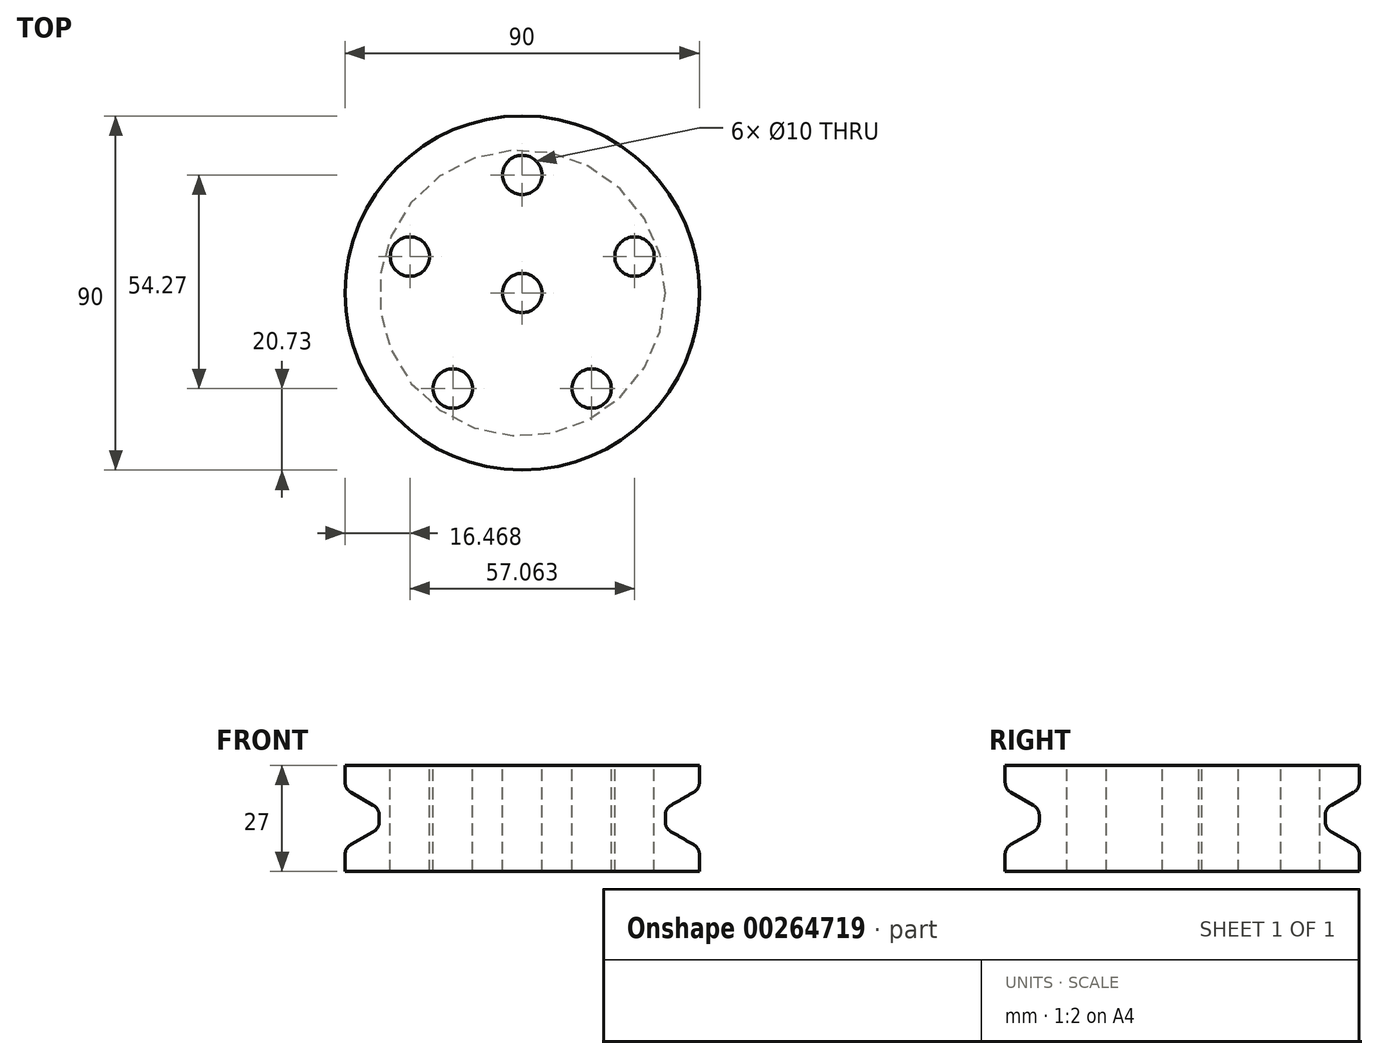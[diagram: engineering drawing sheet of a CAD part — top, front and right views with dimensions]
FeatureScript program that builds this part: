
annotation { "Feature Type Name" : "Feature", "Feature Type Description" : "" }
export const myFeature = defineFeature(function(context is Context, id is Id, definition is map)
    precondition{}
    {
        {
            var Q0;
            Q0=qCreatedBy(makeId("Front.planeOp"),FACE);
            var sketch = newSketch(context, id + "F0", { "sketchPlane" : qUnion([Q0])});
            skLineSegment(sketch, "E0", {"start": v(0, 18.67) * mm, "end": v(0, -19.25) * mm, "construction": true});
            skLineSegment(sketch, "E1", {"start": v(-5, 11.04) * mm, "end": v(-45, 11.04) * mm});
            skLineSegment(sketch, "E2", {"start": v(-45, 11.04) * mm, "end": v(-45, 5.04) * mm});
            skLineSegment(sketch, "E3", {"start": v(-45, 5.04) * mm, "end": v(-36.34, 0.04) * mm});
            skLineSegment(sketch, "E4", {"start": v(-36.34, 0.04) * mm, "end": v(-36.34, -4.96) * mm});
            skLineSegment(sketch, "E5", {"start": v(-36.34, -4.96) * mm, "end": v(-45, -9.96) * mm});
            skLineSegment(sketch, "E6", {"start": v(-45, -9.96) * mm, "end": v(-45, -15.96) * mm});
            skLineSegment(sketch, "E7", {"start": v(-45, -15.96) * mm, "end": v(-5, -15.96) * mm});
            skLineSegment(sketch, "E8", {"start": v(-5, -15.96) * mm, "end": v(-5, 11.04) * mm});
            skSolve(sketch);
        }
        {
            var Q0;
            Q0=makeQuery(id+"F0.imprint","IMPRINT",FACE,{"disambiguationData":[TD([[makeQuery(id+"F0.imprint","IMPRINT",EDGE,{"derivedFrom":sQuery(id+"F0.wireOp",EDGE,"E1")}),1.0]])]});
            var Q1;
            Q1=sQuery(id+"F0.wireOp",EDGE,"E0");
            revolve(context, id + "F1", {"entities" : qUnion([Q0]), "axis" : qUnion([Q1]), "revolveType" : RevolveType.FULL});
        }
        {
            var Q0;
            Q0=makeQuery(id+"F1.opRevolve","SWEPT_FACE",FACE,{"disambiguationData":[OSD([sQuery(id+"F0.wireOp",EDGE,"E1")])]});
            var sketch = newSketch(context, id + "F2", { "sketchPlane" : qUnion([Q0])});
            skCircle(sketch, "E9", {"center": v(0, 30) * mm, "radius": 5 * mm});
            skCircle(sketch, "E10.1.0", {"center": v(-28.53, 9.27) * mm, "radius": 5 * mm});
            skCircle(sketch, "E10.2.0", {"center": v(-17.63, -24.27) * mm, "radius": 5 * mm});
            skCircle(sketch, "E10.3.0", {"center": v(17.63, -24.27) * mm, "radius": 5 * mm});
            skCircle(sketch, "E10.4.0", {"center": v(28.53, 9.27) * mm, "radius": 5 * mm});
            skPoint(sketch, "E10.center", {"position": v(0, 0) * mm});
            skSolve(sketch);
        }
        {
            var Q0;
            Q0=makeQuery(id+"F2.imprint","IMPRINT",FACE,{"disambiguationData":[TD([[makeQuery(id+"F2.imprint","IMPRINT",EDGE,{"derivedFrom":sQuery(id+"F2.wireOp",EDGE,"E10.2.0")}),1.0]])]});
            var Q1;
            Q1=makeQuery(id+"F2.imprint","IMPRINT",FACE,{"disambiguationData":[TD([[makeQuery(id+"F2.imprint","IMPRINT",EDGE,{"derivedFrom":sQuery(id+"F2.wireOp",EDGE,"E10.1.0")}),1.0]])]});
            var Q2;
            Q2=makeQuery(id+"F2.imprint","IMPRINT",FACE,{"disambiguationData":[TD([[makeQuery(id+"F2.imprint","IMPRINT",EDGE,{"derivedFrom":sQuery(id+"F2.wireOp",EDGE,"E9")}),1.0]])]});
            var Q3;
            Q3=makeQuery(id+"F2.imprint","IMPRINT",FACE,{"disambiguationData":[TD([[makeQuery(id+"F2.imprint","IMPRINT",EDGE,{"derivedFrom":sQuery(id+"F2.wireOp",EDGE,"E10.4.0")}),1.0]])]});
            var Q4;
            Q4=makeQuery(id+"F2.imprint","IMPRINT",FACE,{"disambiguationData":[TD([[makeQuery(id+"F2.imprint","IMPRINT",EDGE,{"derivedFrom":sQuery(id+"F2.wireOp",EDGE,"E10.3.0")}),1.0]])]});
            var Q5;
            Q5=makeQuery(id+"F1.opRevolve","SWEPT_FACE",FACE,{"disambiguationData":[OSD([sQuery(id+"F0.wireOp",EDGE,"E7")])]});
            extrude(context, id + "F3", {"entities" : qUnion([Q0, Q1, Q2, Q3, Q4]), "operationType" : NewBodyOperationType.REMOVE, "endBound" : BoundingType.UP_TO_NEXT, "oppositeDirection" : true, "endBoundEntityFace" : qUnion([Q5]), "depth" : 30 * mm});
        }
        {
            var Q0;
            Q0=makeQuery(id+"F1.opRevolve","SWEPT_EDGE",EDGE,{"disambiguationData":[OSD([sQuery(id+"F0.wireOp",EDGE,"E3"),sQuery(id+"F0.wireOp",EDGE,"E4")])]});
            var Q1;
            Q1=makeQuery(id+"F1.opRevolve","SWEPT_FACE",FACE,{"disambiguationData":[OSD([sQuery(id+"F0.wireOp",EDGE,"E4")])]});
            var Q2;
            Q2=makeQuery(id+"F1.opRevolve","SWEPT_EDGE",EDGE,{"disambiguationData":[OSD([sQuery(id+"F0.wireOp",EDGE,"E2"),sQuery(id+"F0.wireOp",EDGE,"E3")])]});
            var Q3;
            Q3=makeQuery(id+"F1.opRevolve","SWEPT_EDGE",EDGE,{"disambiguationData":[OSD([sQuery(id+"F0.wireOp",EDGE,"E5"),sQuery(id+"F0.wireOp",EDGE,"E6")])]});
            fillet(context, id + "F4", {"entities" : qUnion([Q0, Q1, Q2, Q3]), "radius" : 3 * mm, "tangentPropagation" : true, "rho" : 0.5, "crossSection" : FilletCrossSection.CONIC, "allowEdgeOverflow" : false});
        }
    });
